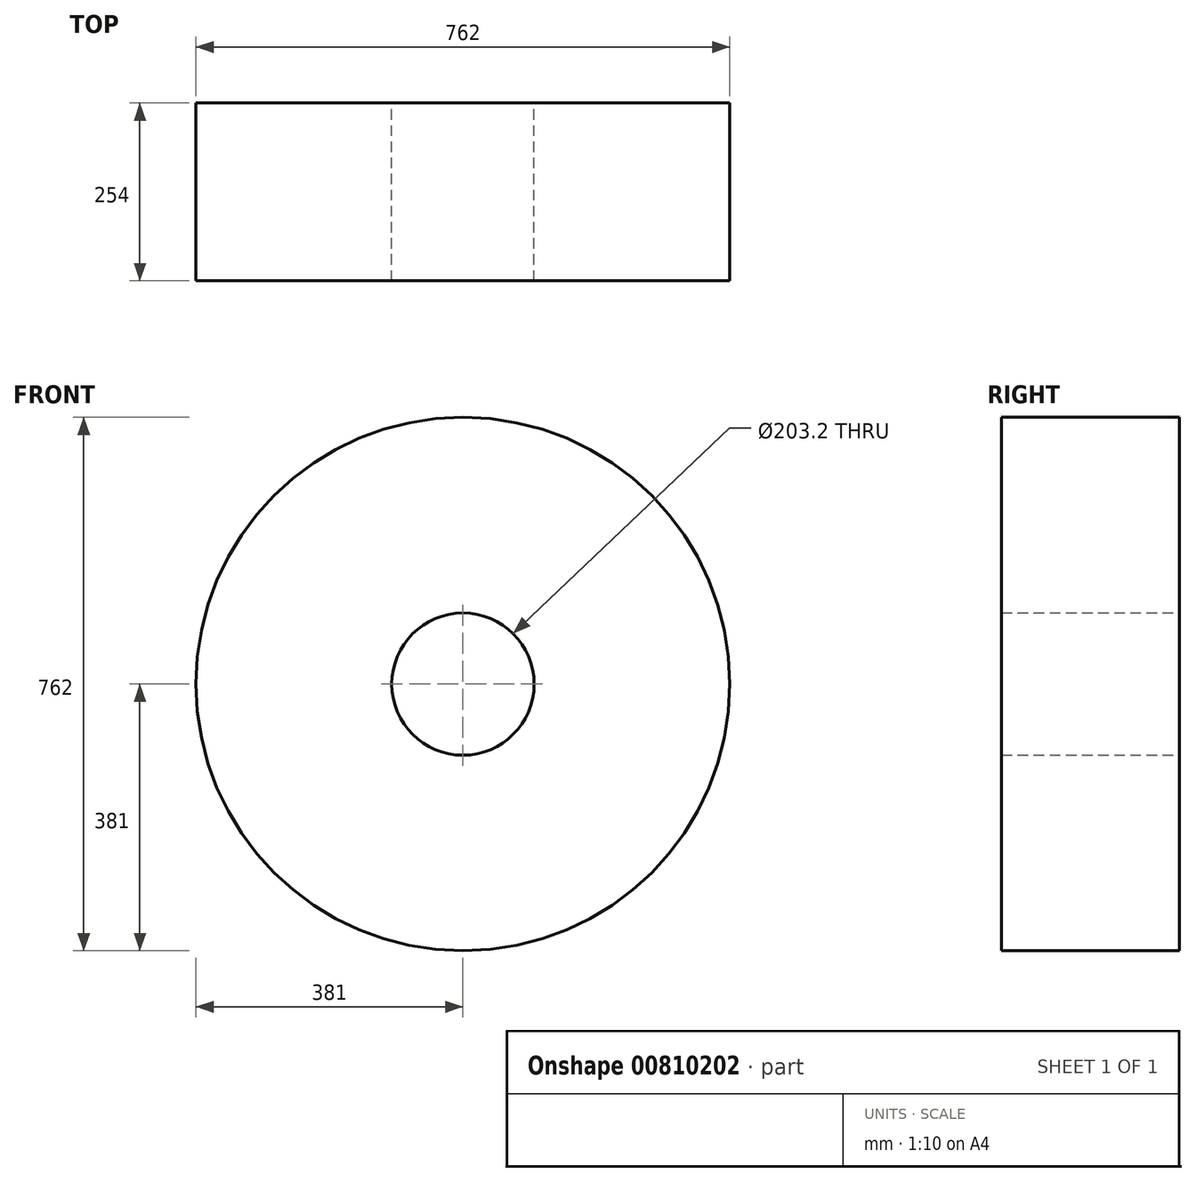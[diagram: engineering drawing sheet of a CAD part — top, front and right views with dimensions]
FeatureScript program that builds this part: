
annotation { "Feature Type Name" : "Feature", "Feature Type Description" : "" }
export const myFeature = defineFeature(function(context is Context, id is Id, definition is map)
    precondition{}
    {
        {
            var Q0;
            Q0=qCreatedBy(makeId("Front.planeOp"),FACE);
            var sketch = newSketch(context, id + "F0", { "sketchPlane" : qUnion([Q0])});
            skCircle(sketch, "E0", {"center": v(0, 0) * mm, "radius": 381 * mm});
            skCircle(sketch, "E1", {"center": v(0, 0) * mm, "radius": 101.6 * mm});
            skSolve(sketch);
        }
        {
            var Q0;
            Q0=makeQuery(id+"F0.imprint","IMPRINT",FACE,{"disambiguationData":[TD([[makeQuery(id+"F0.imprint","IMPRINT",EDGE,{"derivedFrom":sQuery(id+"F0.wireOp",EDGE,"E0")}),1.0]])]});
            extrude(context, id + "F1", {"entities" : qUnion([Q0]), "depth" : 254 * mm, "offsetDistance" : 25.4 * mm});
        }
    });
